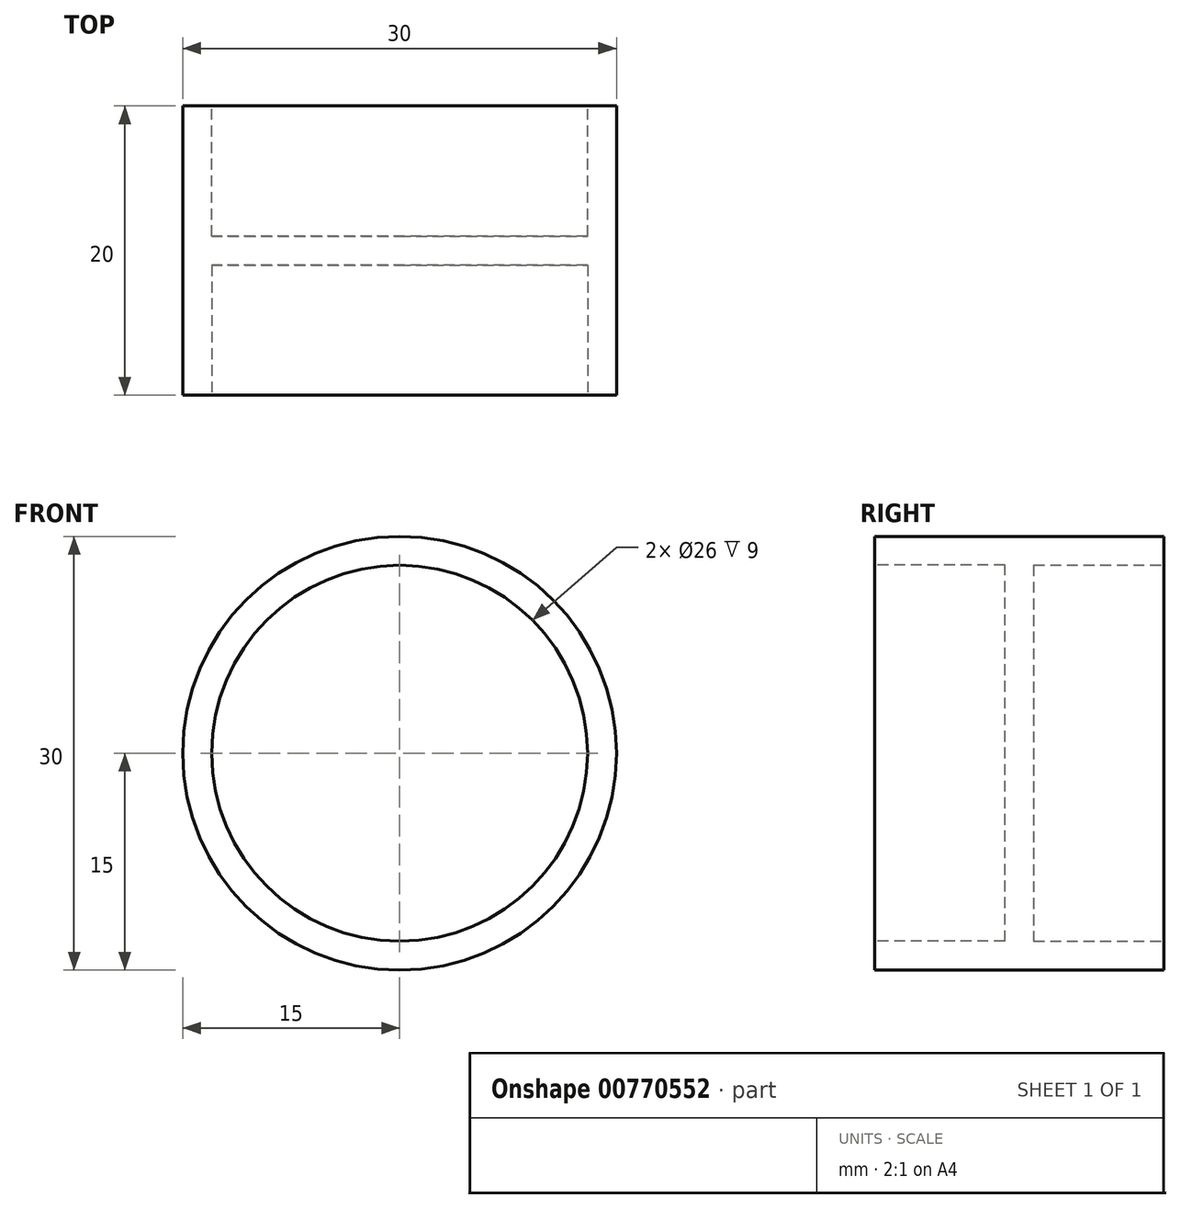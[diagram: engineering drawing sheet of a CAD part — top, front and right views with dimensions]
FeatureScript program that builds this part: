
annotation { "Feature Type Name" : "Feature", "Feature Type Description" : "" }
export const myFeature = defineFeature(function(context is Context, id is Id, definition is map)
    precondition{}
    {
        {
            var Q0;
            Q0=qCreatedBy(makeId("Front.planeOp"),FACE);
            var sketch = newSketch(context, id + "F0", { "sketchPlane" : qUnion([Q0])});
            skCircle(sketch, "E0", {"center": v(0, 0) * mm, "radius": 15 * mm});
            skSolve(sketch);
        }
        {
            var Q0;
            Q0=makeQuery(id+"F0.imprint","IMPRINT",FACE,{"disambiguationData":[TD([[makeQuery(id+"F0.imprint","IMPRINT",EDGE,{"derivedFrom":sQuery(id+"F0.wireOp",EDGE,"E0")}),1.0]])]});
            extrude(context, id + "F1", {"entities" : qUnion([Q0]), "oppositeDirection" : true, "depth" : 20 * mm, "offsetDistance" : 25 * mm});
        }
        {
            var Q0;
            Q0=makeQuery(id+"F1.opExtrude","CAP_FACE",FACE,{"disambiguationData":[OSD([sQuery(id+"F0.wireOp",EDGE,"E0")])],"isStart":true});
            var sketch = newSketch(context, id + "F2", { "sketchPlane" : qUnion([Q0])});
            skCircle(sketch, "E1", {"center": v(0, 0) * mm, "radius": 13 * mm});
            skSolve(sketch);
        }
        {
            var Q0;
            Q0=makeQuery(id+"F2.imprint","IMPRINT",FACE,{"disambiguationData":[TD([[makeQuery(id+"F2.imprint","IMPRINT",EDGE,{"derivedFrom":sQuery(id+"F2.wireOp",EDGE,"E1")}),1.0]])]});
            extrude(context, id + "F3", {"entities" : qUnion([Q0]), "operationType" : NewBodyOperationType.REMOVE, "oppositeDirection" : true, "depth" : 9 * mm, "offsetDistance" : 25 * mm});
        }
        {
            var Q0;
            Q0=makeQuery(id+"F1.opExtrude","CAP_FACE",FACE,{"disambiguationData":[OSD([sQuery(id+"F0.wireOp",EDGE,"E0")])],"isStart":false});
            var sketch = newSketch(context, id + "F4", { "sketchPlane" : qUnion([Q0])});
            skCircle(sketch, "E2", {"center": v(0, 0) * mm, "radius": 13 * mm});
            skSolve(sketch);
        }
        {
            var Q0;
            Q0=makeQuery(id+"F4.imprint","IMPRINT",FACE,{"disambiguationData":[TD([[makeQuery(id+"F4.imprint","IMPRINT",EDGE,{"derivedFrom":sQuery(id+"F4.wireOp",EDGE,"E2")}),1.0]])]});
            extrude(context, id + "F5", {"entities" : qUnion([Q0]), "operationType" : NewBodyOperationType.REMOVE, "oppositeDirection" : true, "depth" : 9 * mm, "offsetDistance" : 25 * mm});
        }
    });
